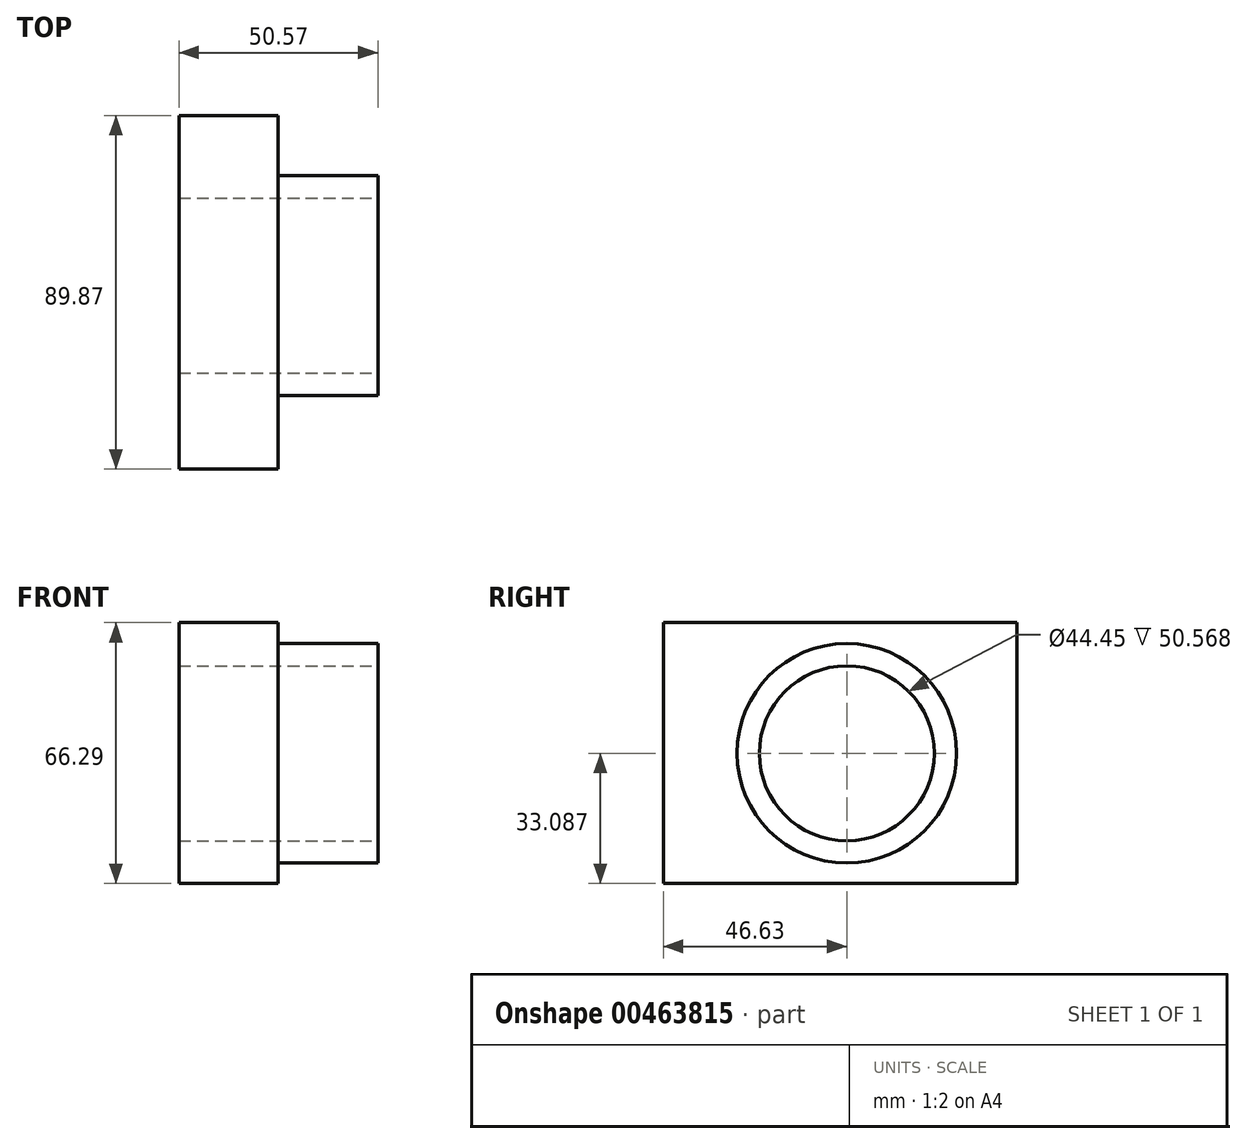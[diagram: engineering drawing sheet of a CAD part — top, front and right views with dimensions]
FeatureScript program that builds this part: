
annotation { "Feature Type Name" : "Feature", "Feature Type Description" : "" }
export const myFeature = defineFeature(function(context is Context, id is Id, definition is map)
    precondition{}
    {
        {
            var Q0;
            Q0=qCreatedBy(makeId("Top.planeOp"),FACE);
            var sketch = newSketch(context, id + "F0", { "sketchPlane" : qUnion([Q0])});
            skLineSegment(sketch, "E0.bottom", {"start": v(25.17, -46.63) * mm, "end": v(0, -46.63) * mm});
            skLineSegment(sketch, "E0.top", {"start": v(25.17, 43.24) * mm, "end": v(0, 43.24) * mm});
            skLineSegment(sketch, "E0.left", {"start": v(25.17, -46.63) * mm, "end": v(25.17, 43.24) * mm});
            skLineSegment(sketch, "E0.right", {"start": v(0, -46.63) * mm, "end": v(0, 43.24) * mm});
            skSolve(sketch);
        }
        {
            var Q0;
            Q0=makeQuery(id+"F0.imprint","IMPRINT",FACE,{"disambiguationData":[TD([[makeQuery(id+"F0.imprint","IMPRINT",EDGE,{"derivedFrom":sQuery(id+"F0.wireOp",EDGE,"E0.bottom")}),-1.0]])]});
            extrude(context, id + "F1", {"entities" : qUnion([Q0]), "depth" : 66.3 * mm});
        }
        {
            var Q0;
            Q0=makeQuery(id+"F1.opExtrude","SWEPT_FACE",FACE,{"disambiguationData":[OSD([sQuery(id+"F0.wireOp",EDGE,"E0.left")])]});
            var sketch = newSketch(context, id + "F2", { "sketchPlane" : qUnion([Q0])});
            skCircle(sketch, "E1", {"center": v(0, 33.09) * mm, "radius": 27.89 * mm});
            skSolve(sketch);
        }
        {
            var Q0;
            Q0=makeQuery(id+"F2.imprint","IMPRINT",FACE,{"disambiguationData":[TD([[makeQuery(id+"F2.imprint","IMPRINT",EDGE,{"derivedFrom":sQuery(id+"F2.wireOp",EDGE,"E1")}),1.0]])]});
            extrude(context, id + "F3", {"entities" : qUnion([Q0]), "operationType" : NewBodyOperationType.ADD, "depth" : 25.4 * mm});
        }
        {
            var Q0;
            Q0=makeQuery(id+"F3.opExtrude","CAP_FACE",FACE,{"disambiguationData":[OSD([sQuery(id+"F2.wireOp",EDGE,"E1")])],"isStart":false});
            var sketch = newSketch(context, id + "F4", { "sketchPlane" : qUnion([Q0])});
            skCircle(sketch, "E2", {"center": v(0, 33.09) * mm, "radius": 17.63 * mm});
            skSolve(sketch);
        }
        {
            var Q0;
            Q0=sQuery(id+"F4.wireOp",VERTEX,"E2.center");
            var Q1;
            Q1=makeQuery(id+"F1.opExtrude","SWEPT_BODY",BODY,{"disambiguationData":[OSD([sQuery(id+"F0.wireOp",EDGE,"E0.bottom"),sQuery(id+"F0.wireOp",EDGE,"E0.top"),sQuery(id+"F0.wireOp",EDGE,"E0.left"),sQuery(id+"F0.wireOp",EDGE,"E0.right")])]});
            hole(context, id + "F5", {"style" : HoleStyle.SIMPLE, "endStyle" : HoleEndStyle.THROUGH, "holeDiameter" : 44.45 * mm, "isTappedThrough" : true, "tappedDepth" : 12.7 * mm, "tapClearance" : 3, "locations" : qUnion([Q0]), "scope" : qUnion([Q1])});
        }
    });
